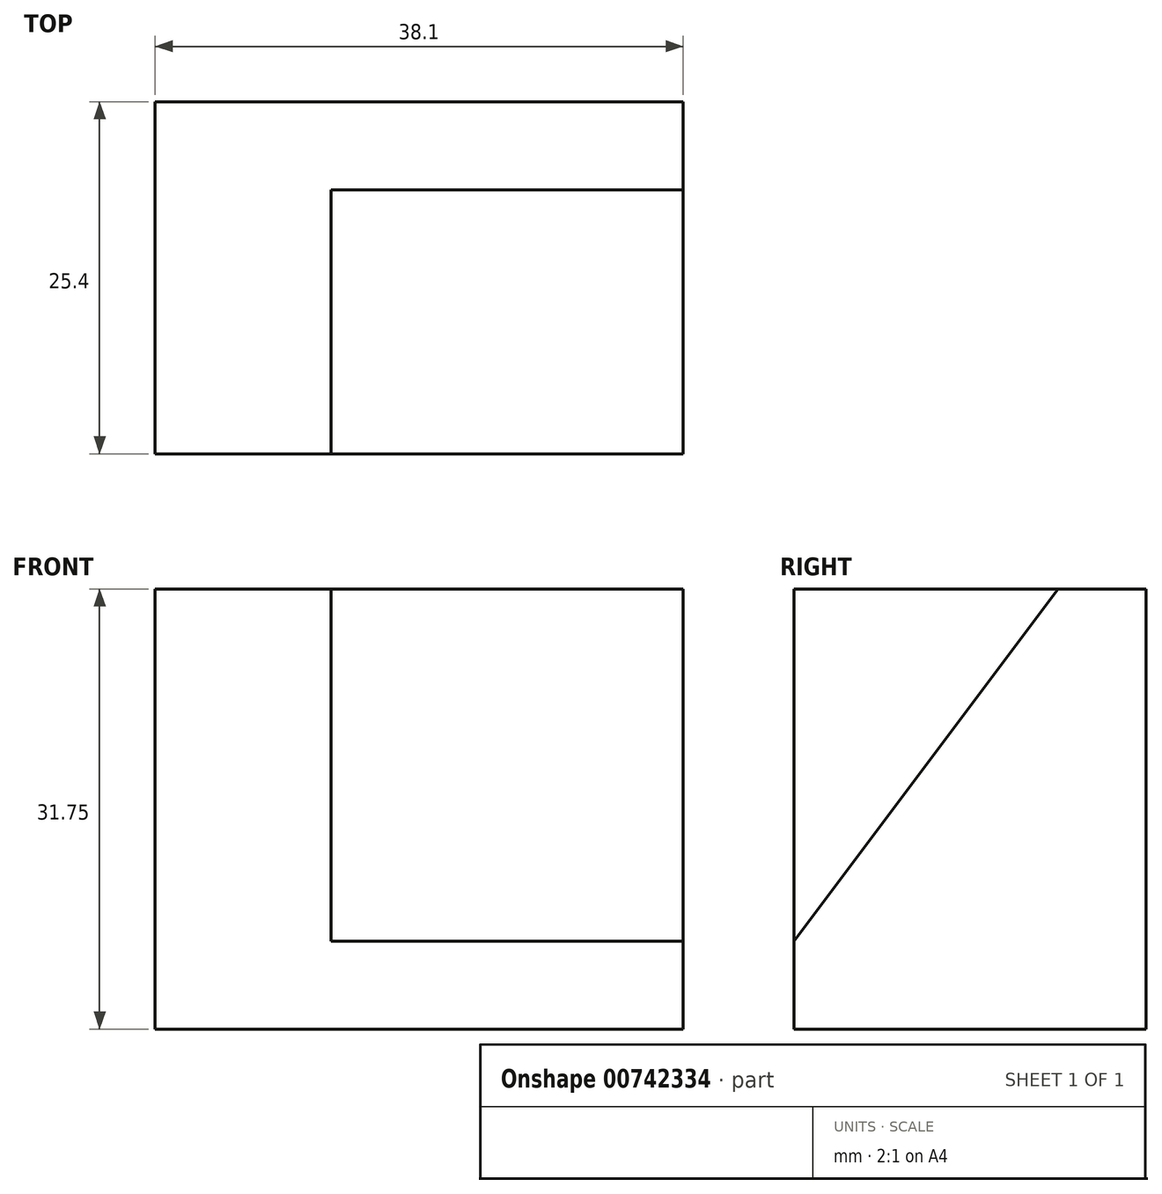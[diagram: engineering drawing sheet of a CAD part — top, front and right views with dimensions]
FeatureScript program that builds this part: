
annotation { "Feature Type Name" : "Feature", "Feature Type Description" : "" }
export const myFeature = defineFeature(function(context is Context, id is Id, definition is map)
    precondition{}
    {
        {
            var Q0;
            Q0=qCreatedBy(makeId("Right.planeOp"),FACE);
            var sketch = newSketch(context, id + "F0", { "sketchPlane" : qUnion([Q0])});
            skLineSegment(sketch, "E0", {"start": v(0, 0) * mm, "end": v(25.4, 0) * mm});
            skLineSegment(sketch, "E1", {"start": v(25.4, 0) * mm, "end": v(25.4, 31.75) * mm});
            skLineSegment(sketch, "E2", {"start": v(25.4, 31.75) * mm, "end": v(0, 31.75) * mm});
            skLineSegment(sketch, "E3", {"start": v(0, 31.75) * mm, "end": v(0, 0) * mm});
            skSolve(sketch);
        }
        {
            var Q0;
            Q0 = qSketchRegion(id + "F0", true);
            extrude(context, id + "F1", {"entities" : qUnion([Q0]), "depth" : 38.1 * mm, "offsetDistance" : 25.4 * mm});
        }
        {
            var Q0;
            Q0=makeQuery(id+"F1.opExtrude","CAP_FACE",FACE,{"disambiguationData":[OSD([sQuery(id+"F0.wireOp",EDGE,"E0"),sQuery(id+"F0.wireOp",EDGE,"E1"),sQuery(id+"F0.wireOp",EDGE,"E2"),sQuery(id+"F0.wireOp",EDGE,"E3")])],"isStart":false});
            var sketch = newSketch(context, id + "F2", { "sketchPlane" : qUnion([Q0])});
            skLineSegment(sketch, "E4", {"start": v(19.05, 31.75) * mm, "end": v(0, 6.35) * mm});
            skSolve(sketch);
        }
        {
            var Q0;
            {var subQ0=sQuery(id+"F2.wireOp",EDGE,"E4");Q0=makeQuery(id+"F2.imprint","IMPRINT",FACE,{"disambiguationData":[TD([[makeQuery(id+"F2.imprint","IMPRINT",EDGE,{"derivedFrom":subQ0}),-1.0]])]});}
            extrude(context, id + "F3", {"entities" : qUnion([Q0]), "operationType" : NewBodyOperationType.REMOVE, "oppositeDirection" : true, "depth" : 25.4 * mm, "offsetDistance" : 25.4 * mm});
        }
    });
